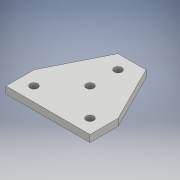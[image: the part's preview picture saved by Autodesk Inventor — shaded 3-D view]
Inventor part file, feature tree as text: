
AUTODESK INVENTOR PART (.ipt)
format: ipt  version: 2018 (Build 220112000, 112)  size: 107,520 bytes
history: native  units: mm
features: extrude x1, sketch x1
ambient origin geometry x8: Origin, YZ Plane, XZ Plane, XY Plane, X Axis, Y Axis, Z Axis, Center Point
bodies: Solid1 (feature_tree)
feature tree (2):
  extrude  "Extrusion1"  Depth=60.0mm
  sketch  "Sketch1"  dims[d0=60.0mm d1=60.0mm d2=20.0mm d3=20.0mm d4=5.5mm d5=10.0mm d6=20.0mm d7=10.0mm d8=10.0mm d9=10.0mm d10=5.0mm d11=0.0mm]
